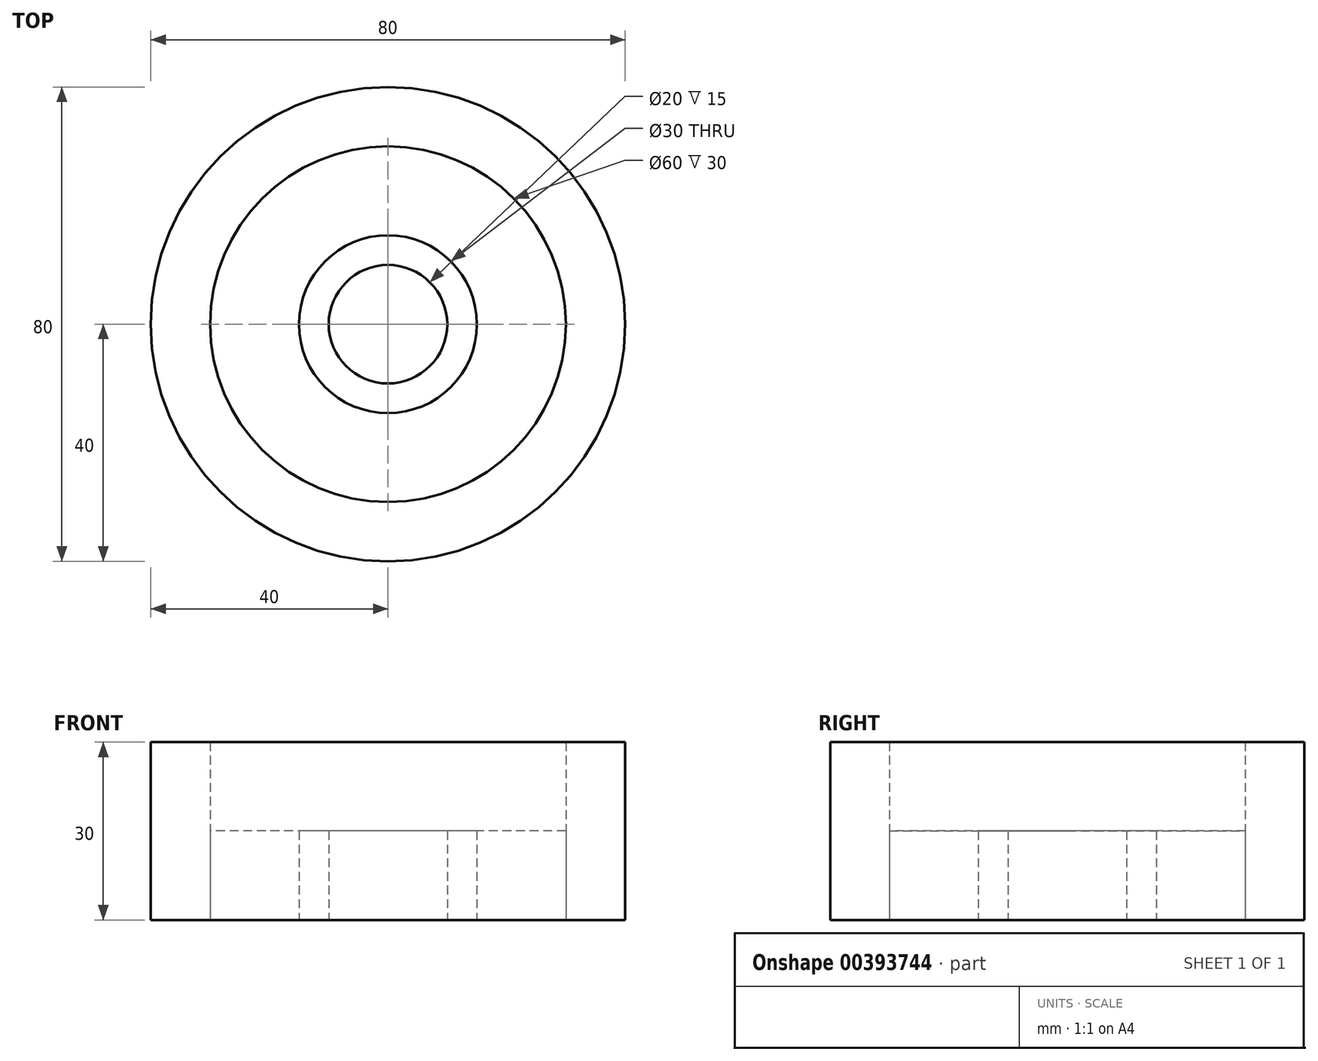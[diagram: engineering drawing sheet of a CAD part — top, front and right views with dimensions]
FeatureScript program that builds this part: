
annotation { "Feature Type Name" : "Feature", "Feature Type Description" : "" }
export const myFeature = defineFeature(function(context is Context, id is Id, definition is map)
    precondition{}
    {
        {
            var Q0;
            Q0=qCreatedBy(makeId("Top.planeOp"),FACE);
            var sketch = newSketch(context, id + "F0", { "sketchPlane" : qUnion([Q0])});
            skCircle(sketch, "E0", {"center": v(0, 0) * mm, "radius": 10 * mm});
            skCircle(sketch, "E1", {"center": v(0, 0) * mm, "radius": 15 * mm});
            skCircle(sketch, "E2", {"center": v(0, 0) * mm, "radius": 30 * mm});
            skCircle(sketch, "E3", {"center": v(0, 0) * mm, "radius": 40 * mm});
            skSolve(sketch);
        }
        {
            var Q0;
            Q0=makeQuery(id+"F0.imprint","IMPRINT",FACE,{"disambiguationData":[TD([[makeQuery(id+"F0.imprint","IMPRINT",EDGE,{"derivedFrom":sQuery(id+"F0.wireOp",EDGE,"E2")}),-1.0]])]});
            extrude(context, id + "F1", {"entities" : qUnion([Q0]), "depth" : 30 * mm});
        }
        {
            var Q0;
            Q0=makeQuery(id+"F0.imprint","IMPRINT",FACE,{"disambiguationData":[TD([[makeQuery(id+"F0.imprint","IMPRINT",EDGE,{"derivedFrom":sQuery(id+"F0.wireOp",EDGE,"E0")}),-1.0]])]});
            extrude(context, id + "F2", {"entities" : qUnion([Q0]), "depth" : 20 * mm});
        }
        {
            var Q0;
            Q0=makeQuery(id+"F0.imprint","IMPRINT",FACE,{"disambiguationData":[TD([[makeQuery(id+"F0.imprint","IMPRINT",EDGE,{"derivedFrom":sQuery(id+"F0.wireOp",EDGE,"E1")}),-1.0]])]});
            extrude(context, id + "F3", {"entities" : qUnion([Q0]), "depth" : 15 * mm});
        }
        {
            var Q0;
            Q0=makeQuery(id+"F2.opExtrude","CAP_FACE",FACE,{"disambiguationData":[OSD([sQuery(id+"F0.wireOp",EDGE,"E0"),sQuery(id+"F0.wireOp",EDGE,"E1")])],"isStart":false});
            extrude(context, id + "F4", {"entities" : qUnion([Q0]), "operationType" : NewBodyOperationType.REMOVE, "oppositeDirection" : true, "depth" : 5 * mm});
        }
    });
